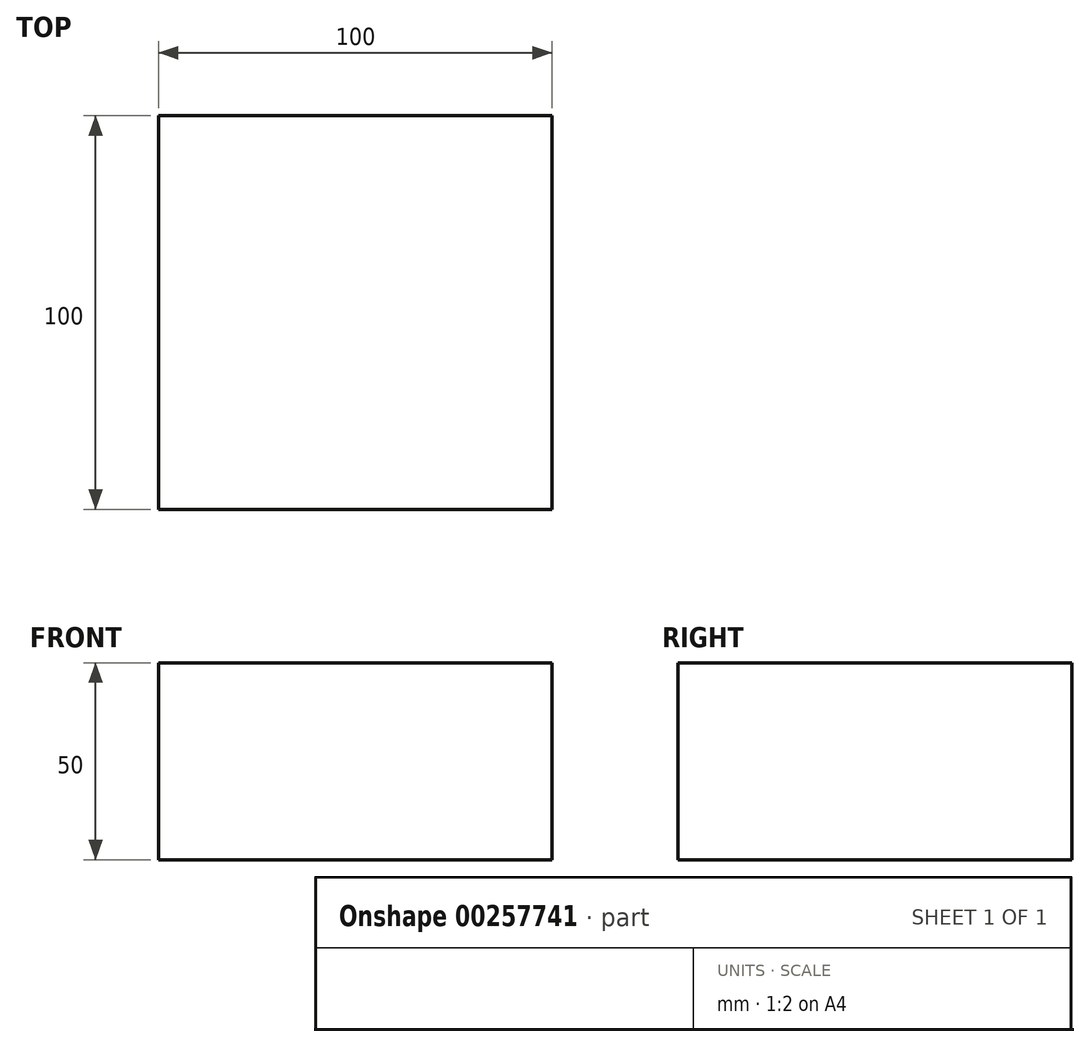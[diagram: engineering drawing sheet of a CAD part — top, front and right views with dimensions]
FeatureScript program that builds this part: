
annotation { "Feature Type Name" : "Feature", "Feature Type Description" : "" }
export const myFeature = defineFeature(function(context is Context, id is Id, definition is map)
    precondition{}
    {
        {
            var Q0;
            Q0=qCreatedBy(makeId("Top.planeOp"),FACE);
            var sketch = newSketch(context, id + "F0", { "sketchPlane" : qUnion([Q0])});
            skLineSegment(sketch, "E0.bottom", {"start": v(0, 0) * mm, "end": v(-100, 0) * mm});
            skLineSegment(sketch, "E0.top", {"start": v(0, -100) * mm, "end": v(-100, -100) * mm});
            skLineSegment(sketch, "E0.left", {"start": v(0, 0) * mm, "end": v(0, -100) * mm});
            skLineSegment(sketch, "E0.right", {"start": v(-100, 0) * mm, "end": v(-100, -100) * mm});
            skSolve(sketch);
        }
        {
            var Q0;
            Q0 = qSketchRegion(id + "F0", true);
            extrude(context, id + "F1", {"entities" : qUnion([Q0]), "depth" : 50 * mm});
        }
    });
